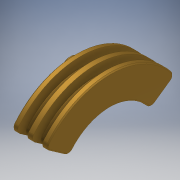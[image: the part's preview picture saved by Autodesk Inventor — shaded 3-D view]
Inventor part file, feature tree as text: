
AUTODESK INVENTOR PART (.ipt)
format: ipt  version: 2018 (Build 220112000, 112)  size: 200,704 bytes
history: native  units: mm
features: extrude x3, sketch x2, pattern_linear x1, fillet x1, chamfer x1
ambient origin geometry x8: Origin, YZ Plane, XZ Plane, XY Plane, X Axis, Y Axis, Z Axis, Center Point
bodies: Body1 (feature_tree)
feature tree (8):
  extrude  "Extrusion1"  Depth=0.6mm TaperAngle=0.0deg
  sketch  "Sketch4"  dims[d18=7.0mm d19=2.0mm d20=1.0mm d21=0.5mm d22=0.0mm d23=3.5mm d24=0.0mm d25=30.0mm d27=1.5mm d28=0.5mm d29=19.198622mm d30=0.1mm d31=2.0mm d32=45.0deg]
  extrude  "Extrusion2"  Depth=2.0mm
  extrude  "Extrusion3"  Depth=1.0mm
  pattern_linear  "Rectangular Pattern1"  Spacing1=0.5mm  [1 undecoded]
  fillet  "Fillet1"  Radius=3.5mm
  chamfer  "Chamfer2"  Distance=1.5mm
  sketch  "Sketch3"  dims[d15=2.0mm d16=0.6mm d17=0.0mm]
note: 1 required parameter value undecoded (feature->parameter linkage not recoverable at this tier; creation-order binding heuristic only, values carry confidence <= 0.55)
